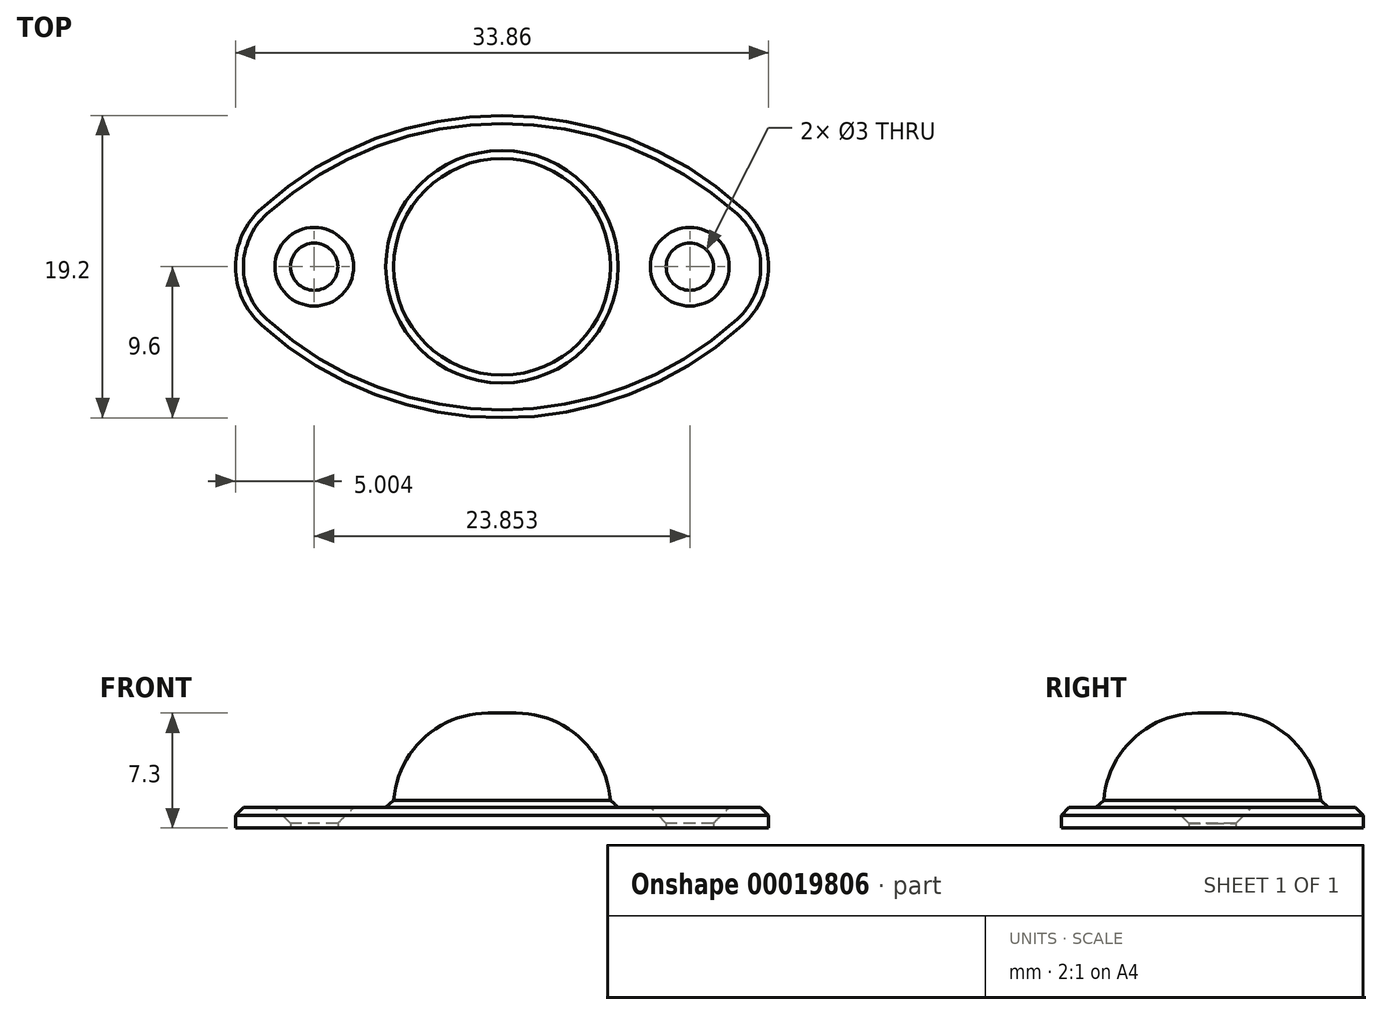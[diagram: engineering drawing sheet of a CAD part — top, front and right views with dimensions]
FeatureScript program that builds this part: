
annotation { "Feature Type Name" : "Feature", "Feature Type Description" : "" }
export const myFeature = defineFeature(function(context is Context, id is Id, definition is map)
    precondition{}
    {
        {
            var Q0;
            Q0=qCreatedBy(makeId("Top.planeOp"),FACE);
            var sketch = newSketch(context, id + "F0", { "sketchPlane" : qUnion([Q0])});
            skArc(sketch, "E0", {"start": v(15.28, 3.7) * mm, "mid": v(0, 9.6) * mm, "end": v(-15.28, 3.7) * mm});
            skLineSegment(sketch, "E1", {"start": v(-18.57, 0) * mm, "end": v(18.57, 0) * mm, "construction": true});
            skArc(sketch, "E2.0.MirrorCS", {"start": v(15.28, -3.7) * mm, "mid": v(0, -9.6) * mm, "end": v(-15.28, -3.7) * mm});
            skPoint(sketch, "E3.visualSharp", {"position": v(-18.57, 0) * mm});
            skArc(sketch, "E3.filletArc", {"start": v(-15.28, 3.7) * mm, "mid": v(-16.93, 0) * mm, "end": v(-15.28, -3.7) * mm});
            skPoint(sketch, "E4.visualSharp", {"position": v(18.57, 0) * mm});
            skArc(sketch, "E4.filletArc", {"start": v(15.28, -3.7) * mm, "mid": v(16.93, 0) * mm, "end": v(15.28, 3.7) * mm});
            skCircle(sketch, "E5", {"center": v(0, 0) * mm, "radius": 6.9 * mm});
            skCircle(sketch, "E6", {"center": v(0, 0) * mm, "radius": 5.85 * mm});
            skCircle(sketch, "E7", {"center": v(11.93, 0) * mm, "radius": 1.5 * mm});
            skCircle(sketch, "E8", {"center": v(-11.93, 0) * mm, "radius": 1.5 * mm});
            skLineSegment(sketch, "E9", {"start": v(6.9, 0) * mm, "end": v(16.93, 0) * mm, "construction": true});
            skLineSegment(sketch, "E10", {"start": v(-1.5, -6.9) * mm, "end": v(1.5, -6.9) * mm});
            skPoint(sketch, "E11", {"position": v(0, -6.9) * mm});
            skSolve(sketch);
        }
        {
            var Q0;
            Q0=makeQuery(id+"F0.imprint","IMPRINT",FACE,{"disambiguationData":[TD([[makeQuery(id+"F0.imprint","IMPRINT",EDGE,{"derivedFrom":sQuery(id+"F0.wireOp",EDGE,"E0")}),1.0]])]});
            extrude(context, id + "F1", {"entities" : qUnion([Q0]), "depth" : 1.3 * mm});
        }
        {
            var Q0;
            Q0=makeQuery(id+"F0.imprint","IMPRINT",FACE,{"disambiguationData":[TD([[makeQuery(id+"F0.imprint","IMPRINT",EDGE,{"derivedFrom":sQuery(id+"F0.wireOp",EDGE,"E5")}),1.0]])]});
            var Q1;
            Q1=makeQuery(id+"F0.imprint","IMPRINT",FACE,{"disambiguationData":[TD([[makeQuery(id+"F0.imprint","IMPRINT",EDGE,{"derivedFrom":sQuery(id+"F0.wireOp",EDGE,"E6")}),1.0]])]});
            extrude(context, id + "F2", {"entities" : qUnion([Q0, Q1]), "operationType" : NewBodyOperationType.ADD, "depth" : 7.3 * mm});
        }
        {
            var Q0;
            Q0=makeQuery(id+"F2.opExtrude","CAP_FACE",FACE,{"disambiguationData":[OSD([sQuery(id+"F0.wireOp",EDGE,"E5")])],"isStart":false});
            fillet(context, id + "F3", {"entities" : qUnion([Q0]), "radius" : 6 * mm, "tangentPropagation" : true, "allowEdgeOverflow" : false});
        }
        {
            var Q0;
            Q0=makeQuery(id+"F1.opExtrude","CAP_EDGE",EDGE,{"disambiguationData":[OSD([sQuery(id+"F0.wireOp",EDGE,"E8")])],"isStart":false});
            var Q1;
            Q1=makeQuery(id+"F1.opExtrude","CAP_EDGE",EDGE,{"disambiguationData":[OSD([sQuery(id+"F0.wireOp",EDGE,"E7")])],"isStart":false});
            chamfer(context, id + "F4", {"entities" : qUnion([Q0, Q1]), "width" : 1 * mm});
        }
        {
            var Q0;
            Q0=makeQuery(id+"F1.opExtrude","CAP_EDGE",EDGE,{"disambiguationData":[OSD([sQuery(id+"F0.wireOp",EDGE,"E0")])],"isStart":false});
            var Q1;
            Q1=makeQuery(id+"F1.opExtrude","CAP_EDGE",EDGE,{"disambiguationData":[OSD([sQuery(id+"F0.wireOp",EDGE,"E3.filletArc")])],"isStart":false});
            chamfer(context, id + "F5", {"entities" : qUnion([Q0, Q1]), "width" : .5 * mm, "tangentPropagation" : true});
        }
        {
            var Q0;
            {var subQ0=sQuery(id+"F0.wireOp",EDGE,"E5");Q0=makeQuery(id+"F3.opFillet","BLEND_EDGE",EDGE,{"blendedFrom":[makeQuery(id+"F2.opExtrude","CAP_EDGE",EDGE,{"disambiguationData":[OSD([subQ0])],"isStart":false}),makeQuery(id+"F1.opExtrude","CAP_FACE",FACE,{"disambiguationData":[OSD([sQuery(id+"F0.wireOp",EDGE,"E0"),sQuery(id+"F0.wireOp",EDGE,"E2.0.MirrorCS"),sQuery(id+"F0.wireOp",EDGE,"E3.filletArc"),sQuery(id+"F0.wireOp",EDGE,"E4.filletArc"),subQ0,sQuery(id+"F0.wireOp",EDGE,"E7"),sQuery(id+"F0.wireOp",EDGE,"E8")])],"isStart":false})],"blendedInto":[makeQuery(id+"F1.opExtrude","CAP_FACE",FACE,{"disambiguationData":[OSD([sQuery(id+"F0.wireOp",EDGE,"E0"),sQuery(id+"F0.wireOp",EDGE,"E2.0.MirrorCS"),sQuery(id+"F0.wireOp",EDGE,"E3.filletArc"),sQuery(id+"F0.wireOp",EDGE,"E4.filletArc"),subQ0,sQuery(id+"F0.wireOp",EDGE,"E7"),sQuery(id+"F0.wireOp",EDGE,"E8")])],"isStart":false})]});}
            chamfer(context, id + "F6", {"entities" : qUnion([Q0]), "width" : .5 * mm, "tangentPropagation" : true});
        }
    });
